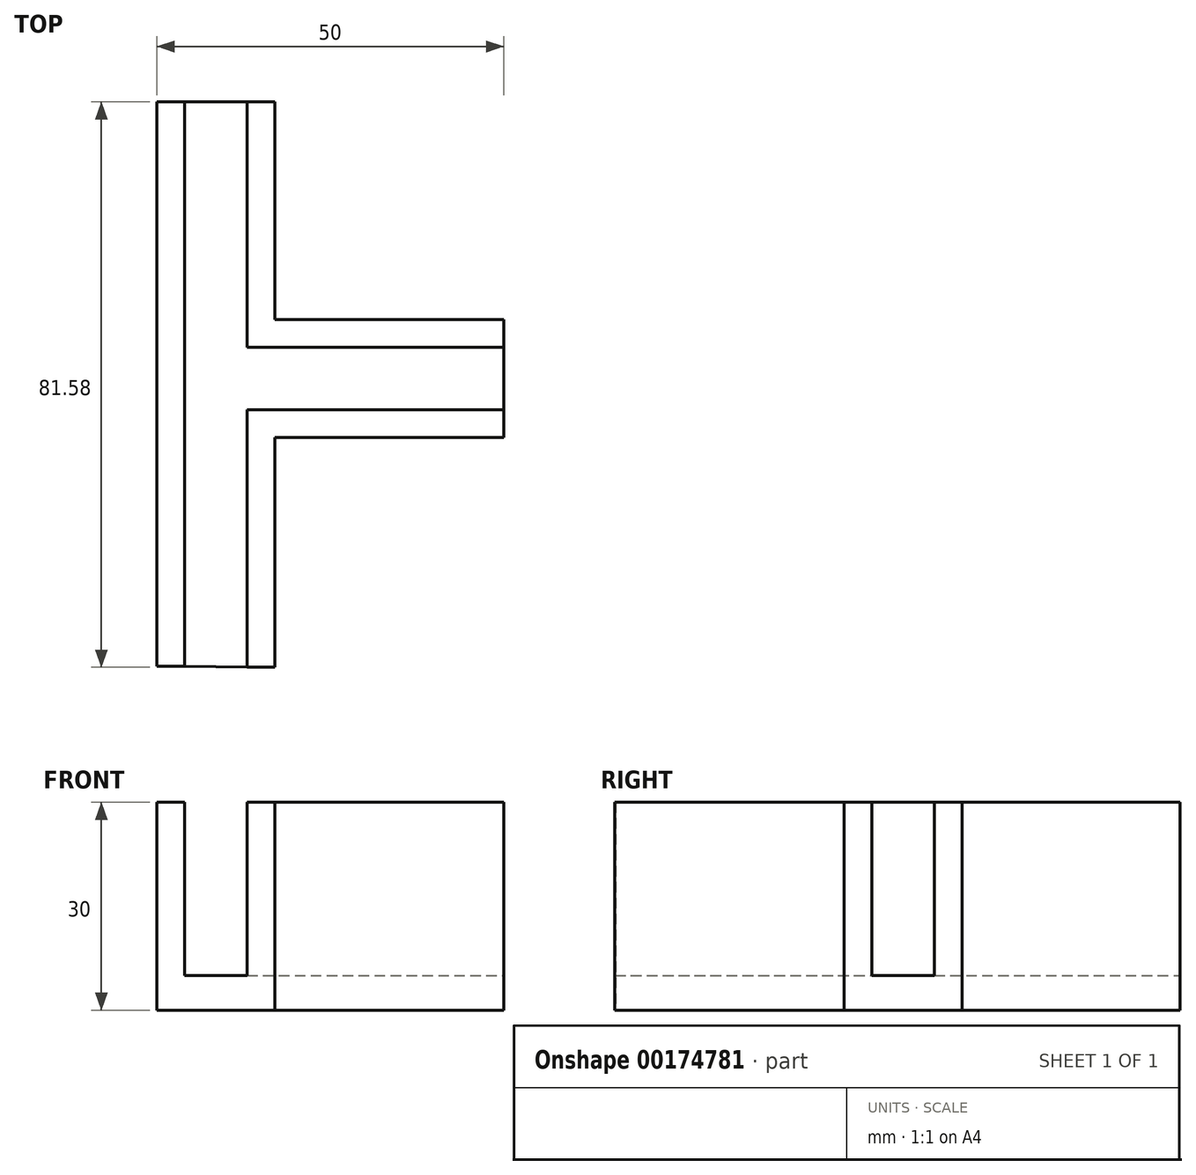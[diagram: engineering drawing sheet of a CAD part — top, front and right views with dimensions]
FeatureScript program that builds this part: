
annotation { "Feature Type Name" : "Feature", "Feature Type Description" : "" }
export const myFeature = defineFeature(function(context is Context, id is Id, definition is map)
    precondition{}
    {
        {
            var Q0;
            Q0=qCreatedBy(makeId("Top.planeOp"),FACE);
            var sketch = newSketch(context, id + "F0", { "sketchPlane" : qUnion([Q0])});
            skLineSegment(sketch, "E0", {"start": v(-23.98, -11.05) * mm, "end": v(-23.98, 38.95) * mm});
            skLineSegment(sketch, "E1", {"start": v(-6.98, 38.95) * mm, "end": v(26.02, 38.95) * mm});
            skLineSegment(sketch, "E2", {"start": v(26.02, 38.95) * mm, "end": v(26.02, 21.95) * mm});
            skLineSegment(sketch, "E3", {"start": v(26.02, 21.95) * mm, "end": v(-6.98, 21.95) * mm});
            skLineSegment(sketch, "E4", {"start": v(-6.98, 21.95) * mm, "end": v(-6.98, -11.19) * mm});
            skLineSegment(sketch, "E5", {"start": v(-6.98, -11.19) * mm, "end": v(-23.98, -11.05) * mm});
            skLineSegment(sketch, "E6", {"start": v(-23.98, 38.95) * mm, "end": v(-23.98, 70.39) * mm});
            skLineSegment(sketch, "E7", {"start": v(-23.98, 70.39) * mm, "end": v(-6.98, 70.39) * mm});
            skLineSegment(sketch, "E8", {"start": v(-6.98, 70.39) * mm, "end": v(-6.98, 38.95) * mm});
            skSolve(sketch);
        }
        {
            var Q0;
            Q0=makeQuery(id+"F0.imprint","IMPRINT",FACE,{"disambiguationData":[TD([[makeQuery(id+"F0.imprint","IMPRINT",EDGE,{"derivedFrom":sQuery(id+"F0.wireOp",EDGE,"E0")}),-1.0]])]});
            extrude(context, id + "F1", {"entities" : qUnion([Q0]), "depth" : 30 * mm});
        }
        {
            var Q0;
            Q0=makeQuery(id+"F1.opExtrude","CAP_FACE",FACE,{"disambiguationData":[OSD([sQuery(id+"F0.wireOp",EDGE,"E0"),sQuery(id+"F0.wireOp",EDGE,"E1"),sQuery(id+"F0.wireOp",EDGE,"E2"),sQuery(id+"F0.wireOp",EDGE,"E3"),sQuery(id+"F0.wireOp",EDGE,"E4"),sQuery(id+"F0.wireOp",EDGE,"E5")])],"isStart":false});
            var sketch = newSketch(context, id + "F2", { "sketchPlane" : qUnion([Q0])});
            skLineSegment(sketch, "E9", {"start": v(-19.98, -11.08) * mm, "end": v(-19.98, 34.95) * mm});
            skLineSegment(sketch, "E10", {"start": v(-10.98, 34.95) * mm, "end": v(26.02, 34.95) * mm});
            skLineSegment(sketch, "E11", {"start": v(-10.98, -11.15) * mm, "end": v(-10.98, 25.95) * mm});
            skLineSegment(sketch, "E12", {"start": v(-10.98, 25.95) * mm, "end": v(26.02, 25.95) * mm});
            skLineSegment(sketch, "E13", {"start": v(-19.98, 34.95) * mm, "end": v(-19.98, 70.39) * mm});
            skLineSegment(sketch, "E14", {"start": v(-10.98, 34.95) * mm, "end": v(-10.98, 70.39) * mm});
            skSolve(sketch);
        }
        {
            var Q0;
            {var subQ3=sQuery(id+"F2.wireOp",EDGE,"E9");Q0=makeQuery(id+"F2.imprint","IMPRINT",FACE,{"disambiguationData":[TD([[makeQuery(id+"F2.imprint","IMPRINT",EDGE,{"derivedFrom":subQ3}),-1.0]])]});}
            extrude(context, id + "F3", {"entities" : qUnion([Q0]), "operationType" : NewBodyOperationType.REMOVE, "oppositeDirection" : true, "depth" : 25 * mm});
        }
    });
